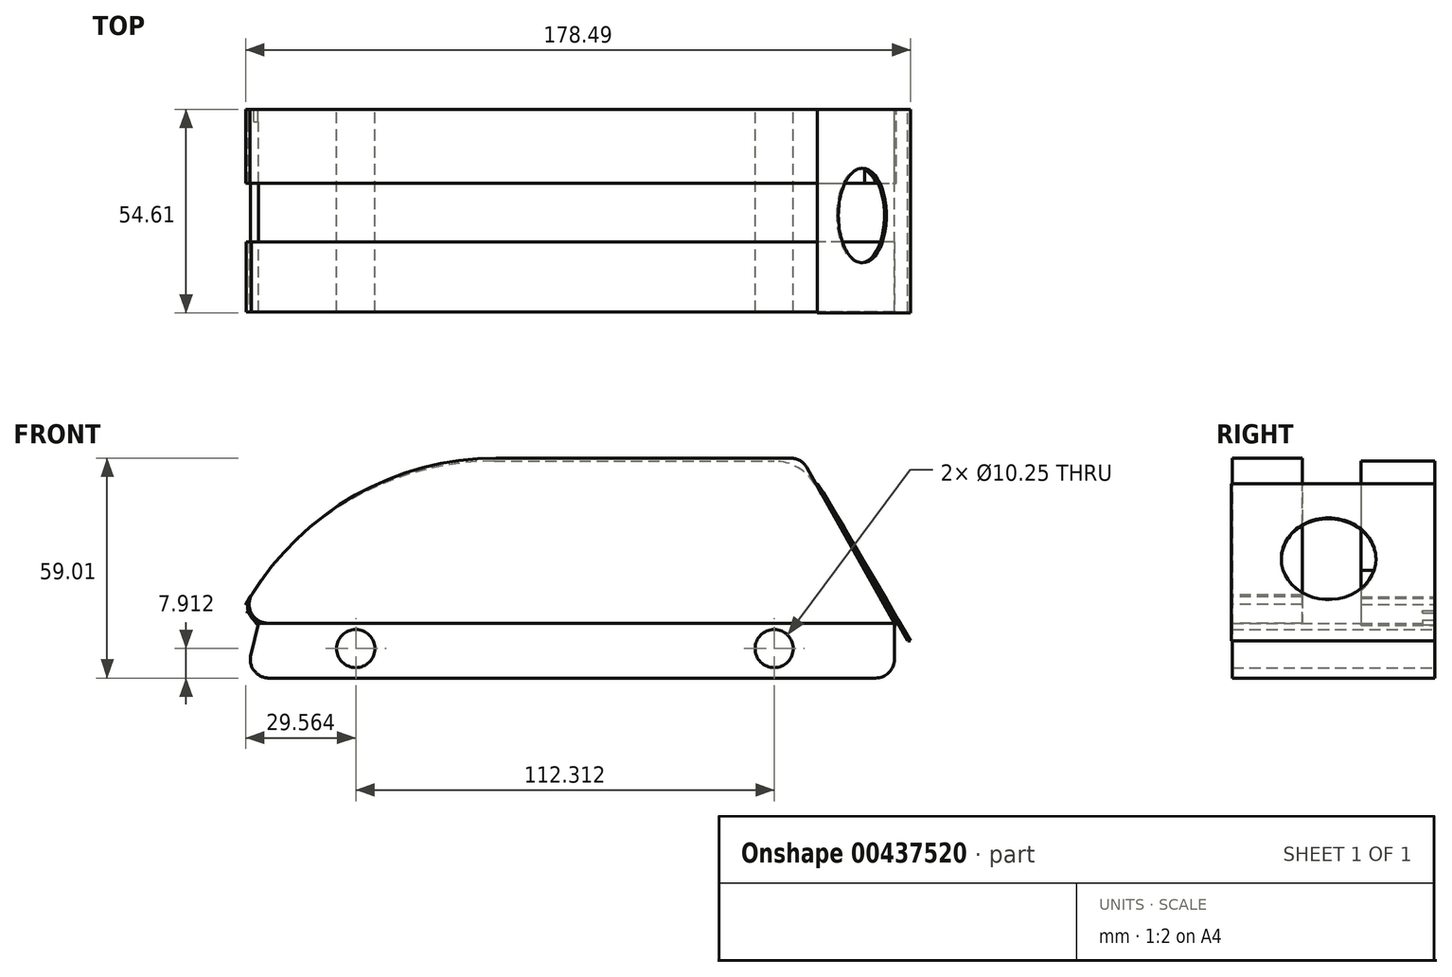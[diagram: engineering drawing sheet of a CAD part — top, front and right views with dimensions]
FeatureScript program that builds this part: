
annotation { "Feature Type Name" : "Feature", "Feature Type Description" : "" }
export const myFeature = defineFeature(function(context is Context, id is Id, definition is map)
    precondition{}
    {
        {
            var Q0;
            Q0=qCreatedBy(makeId("Front.planeOp"),FACE);
            var sketch = newSketch(context, id + "F0", { "sketchPlane" : qUnion([Q0])});
            skLineSegment(sketch, "E0", {"start": v(-19.07, 29) * mm, "end": v(56.17, 29) * mm});
            skLineSegment(sketch, "E1", {"start": v(-84.5, -7.36) * mm, "end": v(-85.72, -9.47) * mm});
            skLineSegment(sketch, "E2.MirrorCS", {"start": v(67.17, 22.66) * mm, "end": v(88.9, -14.98) * mm});
            skLineSegment(sketch, "E3", {"start": v(-80.1, -14.98) * mm, "end": v(88.9, -14.98) * mm});
            skPoint(sketch, "E4.visualSharp", {"position": v(-63.5, 29) * mm});
            skArc(sketch, "E4.filletArc", {"start": v(-19.07, 29) * mm, "mid": v(-57.55, 18.7) * mm, "end": v(-85.72, -9.47) * mm});
            skPoint(sketch, "E5.visualSharp", {"position": v(88.9, -14.98) * mm});
            skLineSegment(sketch, "E5.filletArc", {"start": v(88.9, -14.98) * mm, "end": v(88.9, -14.98) * mm});
            skPoint(sketch, "E6.visualSharp", {"position": v(63.5, 29) * mm});
            skArc(sketch, "E6.filletArc", {"start": v(67.17, 22.66) * mm, "mid": v(62.52, 27.3) * mm, "end": v(56.17, 29) * mm});
            skPoint(sketch, "E7.visualSharp", {"position": v(-88.9, -14.98) * mm});
            skArc(sketch, "E7.filletArc", {"start": v(-84.5, -7.36) * mm, "mid": v(-84.5, -12.44) * mm, "end": v(-80.1, -14.98) * mm});
            skPoint(sketch, "E8.MirrorCS.end.orphan", {"position": v(85.72, -9.47) * mm});
            skPoint(sketch, "E8.MirrorCS.start.orphan", {"position": v(19.07, 29) * mm});
            skSolve(sketch);
        }
        {
            var Q0;
            Q0 = qSketchRegion(id + "F0", true);
            extrude(context, id + "F1", {"entities" : qUnion([Q0]), "depth" : 19.8 * mm});
        }
        {
            var Q0;
            Q0=qCreatedBy(makeId("Front.planeOp"),FACE);
            var sketch = newSketch(context, id + "F2", { "sketchPlane" : qUnion([Q0])});
            skLineSegment(sketch, "E9", {"start": v(88.4, -14.48) * mm, "end": v(88.4, -24.13) * mm});
            skLineSegment(sketch, "E10", {"start": v(83.31, -29.21) * mm, "end": v(-79.4, -29.21) * mm});
            skLineSegment(sketch, "E11", {"start": v(88.4, -14.48) * mm, "end": v(-82.3, -14.48) * mm});
            skLineSegment(sketch, "E12", {"start": v(-82.3, -14.48) * mm, "end": v(-84.34, -22.94) * mm});
            skCircle(sketch, "E13", {"center": v(-56.16, -21.3) * mm, "radius": 5.12 * mm});
            skCircle(sketch, "E14.MirrorC", {"center": v(56.16, -21.3) * mm, "radius": 5.12 * mm});
            skPoint(sketch, "E15.visualSharp", {"position": v(-85.85, -29.21) * mm});
            skArc(sketch, "E15.filletArc", {"start": v(-84.34, -22.94) * mm, "mid": v(-83.4, -27.28) * mm, "end": v(-79.4, -29.21) * mm});
            skPoint(sketch, "E16.visualSharp", {"position": v(88.4, -29.21) * mm});
            skArc(sketch, "E16.filletArc", {"start": v(83.31, -29.21) * mm, "mid": v(86.9, -27.72) * mm, "end": v(88.4, -24.13) * mm});
            skSolve(sketch);
        }
        {
            var Q0;
            Q0 = qSketchRegion(id + "F2", true);
            extrude(context, id + "F3", {"entities" : qUnion([Q0]), "operationType" : NewBodyOperationType.ADD, "depth" : 54.36 * mm});
        }
        {
            var Q0;
            Q0=qCreatedBy(makeId("Front.planeOp"),FACE);
            var sketch = newSketch(context, id + "F4", { "sketchPlane" : qUnion([Q0])});
            skLineSegment(sketch, "E17", {"start": v(-64.66, -16.1) * mm, "end": v(87.74, -16.1) * mm});
            skLineSegment(sketch, "E18", {"start": v(87.74, -16.1) * mm, "end": v(66.38, 23.24) * mm});
            skLineSegment(sketch, "E19.MirrorCS", {"start": v(-85.35, -11.68) * mm, "end": v(-83.67, -8.59) * mm});
            skLineSegment(sketch, "E20", {"start": v(-64.66, -16.1) * mm, "end": v(-79.2, -16.1) * mm});
            skLineSegment(sketch, "E21", {"start": v(-17.72, 28.55) * mm, "end": v(57.46, 28.55) * mm});
            skPoint(sketch, "E22.visualSharp", {"position": v(-63.5, 28.55) * mm});
            skArc(sketch, "E22.filletArc", {"start": v(-17.72, 28.55) * mm, "mid": v(-57.06, 17.73) * mm, "end": v(-85.35, -11.68) * mm});
            skPoint(sketch, "E23.visualSharp", {"position": v(63.5, 28.55) * mm});
            skArc(sketch, "E23.filletArc", {"start": v(66.38, 23.24) * mm, "mid": v(62.65, 27.12) * mm, "end": v(57.46, 28.55) * mm});
            skPoint(sketch, "E24.visualSharp", {"position": v(-87.74, -16.1) * mm});
            skArc(sketch, "E24.filletArc", {"start": v(-83.67, -8.59) * mm, "mid": v(-83.57, -13.6) * mm, "end": v(-79.2, -16.1) * mm});
            skSolve(sketch);
        }
        {
            var Q0;
            Q0 = qSketchRegion(id + "F4", true);
            extrude(context, id + "F5", {"entities" : qUnion([Q0]), "operationType" : NewBodyOperationType.ADD, "depth" : 3.3 * mm});
        }
        {
            var Q0;
            Q0=makeQuery(id+"F3.opExtrude","CAP_FACE",FACE,{"disambiguationData":[OSD([sQuery(id+"F2.wireOp",EDGE,"E9"),sQuery(id+"F2.wireOp",EDGE,"E10"),sQuery(id+"F2.wireOp",EDGE,"E11"),sQuery(id+"F2.wireOp",EDGE,"E12")])],"isStart":false});
            var sketch = newSketch(context, id + "F6", { "sketchPlane" : qUnion([Q0])});
            skLineSegment(sketch, "E25", {"start": v(-82.3, -14.48) * mm, "end": v(88.4, -14.48) * mm});
            skLineSegment(sketch, "E26", {"start": v(88.4, -14.48) * mm, "end": v(64.96, 27.21) * mm});
            skLineSegment(sketch, "E27.MirrorCS", {"start": v(-85.56, -9.45) * mm, "end": v(-84.14, -6.91) * mm});
            skLineSegment(sketch, "E28", {"start": v(-79.7, -14.48) * mm, "end": v(-82.3, -14.48) * mm});
            skLineSegment(sketch, "E29", {"start": v(-18.47, 29.8) * mm, "end": v(60.53, 29.8) * mm});
            skPoint(sketch, "E30.visualSharp", {"position": v(-63.5, 29.8) * mm});
            skArc(sketch, "E30.filletArc", {"start": v(-18.47, 29.8) * mm, "mid": v(-57.34, 19.27) * mm, "end": v(-85.56, -9.45) * mm});
            skPoint(sketch, "E31.visualSharp", {"position": v(63.5, 29.8) * mm});
            skArc(sketch, "E31.filletArc", {"start": v(64.96, 27.21) * mm, "mid": v(63.1, 29.1) * mm, "end": v(60.53, 29.8) * mm});
            skPoint(sketch, "E32.visualSharp", {"position": v(-88.4, -14.48) * mm});
            skArc(sketch, "E32.filletArc", {"start": v(-84.14, -6.91) * mm, "mid": v(-84.1, -11.97) * mm, "end": v(-79.7, -14.48) * mm});
            skSolve(sketch);
        }
        {
            var Q0;
            Q0 = qSketchRegion(id + "F6", true);
            extrude(context, id + "F7", {"entities" : qUnion([Q0]), "oppositeDirection" : true, "depth" : 18.8 * mm});
        }
        {
            var Q0;
            Q0=qCreatedBy(makeId("Front.planeOp"),FACE);
            var sketch = newSketch(context, id + "F8", { "sketchPlane" : qUnion([Q0])});
            skEllipticalArc(sketch, "E33", {});
            skPoint(sketch, "E34", {"position": v(92.04, -19.21) * mm});
            skPoint(sketch, "E35", {"position": v(92.77, -19.21) * mm});
            skLineSegment(sketch, "E36", {"start": v(92.77, -19.21) * mm, "end": v(92.04, -19.21) * mm});
            const initialGuessF8  = {"E33": [0.09054291248321533, -0.016024651005864143, -0.5045222703143845, 0.8633986789176941, 0.0451588479596695, 0.00031737902187038713, 4.626481102648193, 1.6484906361187586]};
            skSetInitialGuess(sketch, initialGuessF8);
            skSolve(sketch);
        }
        {
            var Q0;
            Q0 = qSketchRegion(id + "F8", true);
            extrude(context, id + "F9", {"entities" : qUnion([Q0]), "depth" : 54.6 * mm});
        }
        {
            var Q0;
            Q0=makeQuery(id+"F7.opExtrude","SWEPT_FACE",FACE,{"disambiguationData":[OSD([sQuery(id+"F6.wireOp",EDGE,"E26")])]});
            var sketch = newSketch(context, id + "F10", { "sketchPlane" : qUnion([Q0])});
            skCircle(sketch, "E37", {"center": v(-28.5, -36.65) * mm, "radius": 12.7 * mm});
            skSolve(sketch);
        }
        {
            var Q0;
            Q0 = qSketchRegion(id + "F10", true);
            extrude(context, id + "F11", {"entities" : qUnion([Q0]), "operationType" : NewBodyOperationType.REMOVE, "depth" : 2.03 * mm});
        }
    });
